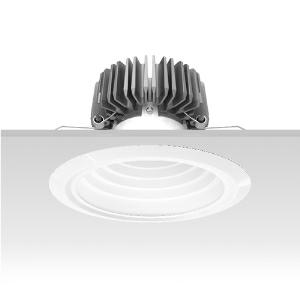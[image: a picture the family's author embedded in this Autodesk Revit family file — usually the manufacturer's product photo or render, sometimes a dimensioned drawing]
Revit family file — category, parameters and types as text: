
# Revit family: 3f_filippi_-_3f_reno_bianco_ampio_3f_filippi_-_30671_a01025_-_3f_reno_200_wh_2000-840_dali_wide___vt_wh_b39a
name_source: partatom
category: Lighting Fixtures
units: mm (PartAtom-declared; Revit-internal decimal feet)

## family parameters
Cut with Voids When Loaded = No
Host = Face
Light Source = No
Part Type = Normal
Room Calculation Point = No
Round Connector Dimension = Use Diameter
Shared = No

## types (1)
- 3F Filippi - 3F Reno Bianco Ampio (1 x LED, 1884 lm, 20 W, 4000 K)
    Apparent Load = 20 VA
    Approval mark = CE
    CIE Flux Codes = 75 94 99 100 100
    Color Rendering = 80
    Color Temperature = 4000 K
    Control Gear = Electronic transformer
    Default Elevation = 1800 mm
    Description = ILLUMINOTECHNICAL
Luminous efficiency 100% (DLOR 100%, ULOR 0%).
Initial luminous flux of the luminaire 1884 lm.
Direct symmetric wide distribution.
Installation Interdistance Transv.D = 1.56 x hu - Long.D = 1.56 x hu.
Average luminance <3000 cd/m² for radial angles >65°.
Tabular UGR (CIE 117 - 4H-8H; S=0.25H; 70/50/20): RUG 20.8 - 20.6.
Beam angle: 74° - 74°.
Luminous efficacy 94 lm/W.
Lifetime (L90/B10): 30000 h. (tq+25°C)
Lifetime (L85/B10): 50000 h. (tq+25°C)
Lifetime (L70/B10): 80000 h. (tq+25°C)
Sudden decreased luminous flux after 50000 hours: 0% (C0).
Photobiological safety in compliance with IEC/TR 62778: RG0 risk exempt, (IEC 62471).
In compliance with IEC/EN 62722-2-1 - IEC/EN 62717 standards.

SOURCE
Compact LED module 2000/840.
Energy efficiency class (UE 2019/2020 - UE 2019/2015): D.
CIE 13.3 Colour rendering index: CRI >80 (R9 <50%).
IES TM-30 Fidelity Index: Rf = 84 Rg = 95.
CCT nominal colour temperature 4000 K.
Colour initial tolerance (MacAdam): SDCM 3.
Zhaga Book 3 compliant.

MECHANICAL
Passive heat dissipator in die-casting aluminium, oversized, for optimum thermal management of the LED module.
Parabolic element with graduated/concentric rings in white polycarbonate.
Transparent external lens with glossy and satin differentiated surfaces, with a cooling and anti-insect system in methacrylate (PMMA).
Fastening spring clips in stainless steel.
Dimensions: diameter 226 mm, height 146 mm. Weight 1.16 kg.
IP44 protection degree for exposed part, IP20 for recessed part.
Mechanical strength to impacts IK06 (1 joule).
Glow-wire test resistance 650°C.

ELECTRICAL
Wiring on a separate unit.
Halogen Free DALI-2 DATI (Parts 251, 252, 253), PUSH-DIM, electronic wiring 230V-50/60Hz, power factor 0.90 at full load, THD <25%, constant output current, SELV, class II, 1 driver, 1 DALI addresse.
Power of the luminaire 20 W.
ENEC - CE.
SAFE FLICKER: PstLM=<1 and SVM=<0.4 (IEC TR 61547-1 and IEC TR 63158), to ensure a more comfortable and safe light.
Luminaire compliant with EN 60598-2-22 for power supply from a centralised emergency system CPSS (Central Power Supply System), not incorporated in the luminaire - high risk areas excluded. The default power and flux are 100% in AC and 100% in DC.
Ambient temperature from 0°C to +25°C.
Temperature class T6 max 85°C.
Relative humidity UR: <85%.

INSTALLATION
Pull-up recessed fitting.
False ceiling carving: 200 mm.
All accessories dedicated to this product are available on the Catalog and on our website www.3F-Filippi.com.

ACCESSORIES
A01025 - VT transparent glass, tempered, not flammable, locked and in line with the trim, in white polycarbonate.

APPLICATIONS
Environments: architectural, commercial, exhibition areas, transit areas, corridors, shops, display windows, service areas.
In false ceilings with narrow voids.

LIGHT MANAGEMENT
Recommended minimum setting: 10%.
The luminaire, equipped with (DALI-2 DATI) driver, can be controlled manually with 3F Easy Dim technology or automatically/manually with wired or wireless DALI/D2D control systems.
The D2D driver guarantees interoperability with other devices with the same certification by making the following information available:
Device Data (Part 251), Energy Report (Part 252), Diagnosis & Maintenance (Part 253).
In electrical systems without a regulation system (manual or automatic) and DALI bus, a suitable jumper must be made on the DA-DA terminals of the appliance.

WARNING
Luminaire designed for disposal/recycling at end-of-life.
Replaceable (LED only) light source by a professional. Replaceable control gear by a professional.
    Height = 0 mm  [stored 0 ft]
    Lamp = 1 x LED
    Lamp Light Flux = 1884 lm
    Lamp Power = 20 W
    Lamp count = 1
    Length = 226 mm
    Lifetime = 50000 h
    Luminous efficacy = 94 lm/W
    Manufacturer = 3F Filippi
    ModVariant = No
    Model = 3F Filippi - 30671+A01025 - 3F Reno 200 WH 2000-840 DALI WIDE + VT WH
    Mounting Place = Ceiling
    Mounting Type = Recessed
    Number of Poles = 1
    OnlyDefault = Yes
    Power Factor = 1
    Product Name = 3F Filippi - 3F Reno Bianco Ampio
    Product group = recessed luminaire
    ProductGroupID = 4
    Protection Class = Protection class II
    Protection Degree = IP 20
    RLX_Detail_Level = 1
    RLX_Emergency_Light_Flux = 0 lm
    RLX_Emergency_Type = 0
    RLX_Emergency_Type_DB = No
    RlxData = <blob elided: 98137 chars, md5=2694f2d1>
    Socket = socket
    Standby Power = 0 W
    System Light Flux = 1884 lm
    System Power = 20 W
    Type Comments = Product without accessories
    Type Image = 3ffilippi_3f_reno_200_wh__a01025.jpg
    URL = http://relux.com
    VarID = ---
    Voltage = 0 V
    Weight = 0.00 kg
    Width = 0 mm  [stored 0 ft]

note: [stored X ft] marks values corroborated as IEEE doubles in the binary element streams (Revit-internal decimal feet)

## geometry (parser evidence)
native form markers: Blend x4, Sweep x9
no freeform markers — native parametric forms only
